# Revit family: Gira_114502
name_source: partatom
category: Electrical Fixtures
revit_build: Autodesk Revit 2017 (Build: 20160225_1515(x64)
units: mm (PartAtom-declared; Revit-internal decimal feet)

## family parameters
Cut with Voids When Loaded = No
Host = Face
Maintain Annotation Orientation = No
Part Type = Normal
Room Calculation Point = No
Round Connector Dimension = Use Diameter
Shared = No

## types (1)
- RWM Basic Q Rauchwarnmelder Reinweiß
    Art des Test-/Pauseknopfes = Prüftaste
    Available = Yes
    Category = Brandmelder
    Data sheet (1) = https://katalog.gira.de
    Default Elevation = 1219 mm
    Durchmesser = 0.125 m
    Explosionsgeprüfte Ausführung = No
    Farbe = weiß
    GTIN = 4010337013525
    Geeignet für Kanalbefestigung = No
    HAN = 114502
    HeinzeBIM = https://bimportal.heinze.de
    Höhe = 0.0385 m
    Kabeleinführung = Unterseite
    Keynote = Rauchwarnmelder
    Lautstärke = 85 dB(A)
    Manufacturer URL = https://www.gira.de
    Mit Backup-Batterie = No
    Mit Orientierungsbeleuchtung = No
    Mit Sockel = Yes
    Mit Spannungsanzeige = No
    Mitgelieferte Backup-Batterie = ohne
    Montageart = Aufbau
    Name = RWM Basic Q Rauchwarnmelder Reinweiß
    Primärstromversorgung = Batterie/Akku
    Rauchschalter = No
    Region = DE
    Schutzart (IP) = IP42
    Spannungsart der Versorgungsspannung = Ac (*en-EN)
    Standalone = Yes
    URL = http://katalog.gira.de
    VdS anerkannt = No
    Vernetzbar über Funk (optional) = No
    Vernetzbar über Funk (standardmäßig) = No
    Vernetzbar über Kabel = No
    Versorgungsspannung = 9 - 9
    Wirkprinzip = optisch

## geometry (parser evidence)
native form markers: Blend x2, Sweep x2
no freeform markers — native parametric forms only
